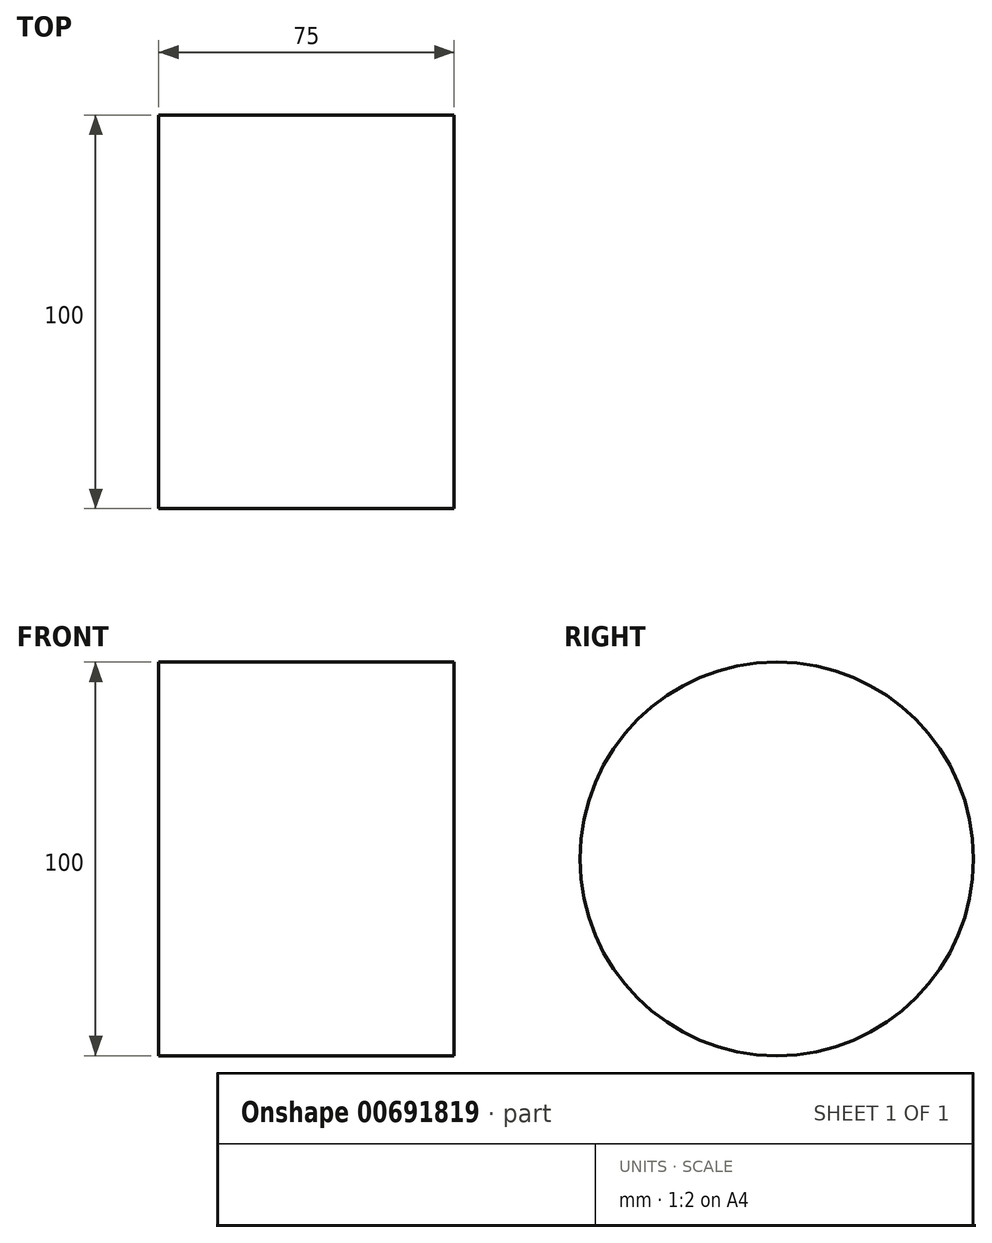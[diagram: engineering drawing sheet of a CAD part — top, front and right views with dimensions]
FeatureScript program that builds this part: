
annotation { "Feature Type Name" : "Feature", "Feature Type Description" : "" }
export const myFeature = defineFeature(function(context is Context, id is Id, definition is map)
    precondition{}
    {
        {
            var Q0;
            Q0=qCreatedBy(makeId("Right.planeOp"),FACE);
            var sketch = newSketch(context, id + "F0", { "sketchPlane" : qUnion([Q0])});
            skCircle(sketch, "E0", {"center": v(0, 0) * mm, "radius": 50 * mm});
            skSolve(sketch);
        }
        {
            var Q0;
            Q0=makeQuery(id+"F0.imprint","IMPRINT",FACE,{"disambiguationData":[TD([[makeQuery(id+"F0.imprint","IMPRINT",EDGE,{"derivedFrom":sQuery(id+"F0.wireOp",EDGE,"E0")}),1.0]])]});
            extrude(context, id + "F1", {"entities" : qUnion([Q0]), "depth" : 75 * mm, "offsetDistance" : 25 * mm});
        }
    });
